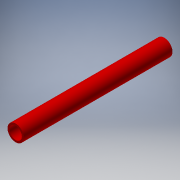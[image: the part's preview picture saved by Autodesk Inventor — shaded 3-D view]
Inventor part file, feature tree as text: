
AUTODESK INVENTOR PART (.ipt)
format: ipt  version: 2018 (Build 220112000, 112)  size: 107,008 bytes
history: native  units: in
note: dims shown in document units (in); Inventor stores cm internally (conversion verified against a paired STEP export)
features: extrude x1, sketch x1
ambient origin geometry x8: Origin, YZ Plane, XZ Plane, XY Plane, X Axis, Y Axis, Z Axis, Center Point
bodies: Solid1 (feature_tree)
feature tree (2):
  extrude  "Extrusion1"  Depth=12.0in
  sketch  "Sketch1"  dims[d0=1.315in d1=1.0in d2=12.0in d3=0.0in]
